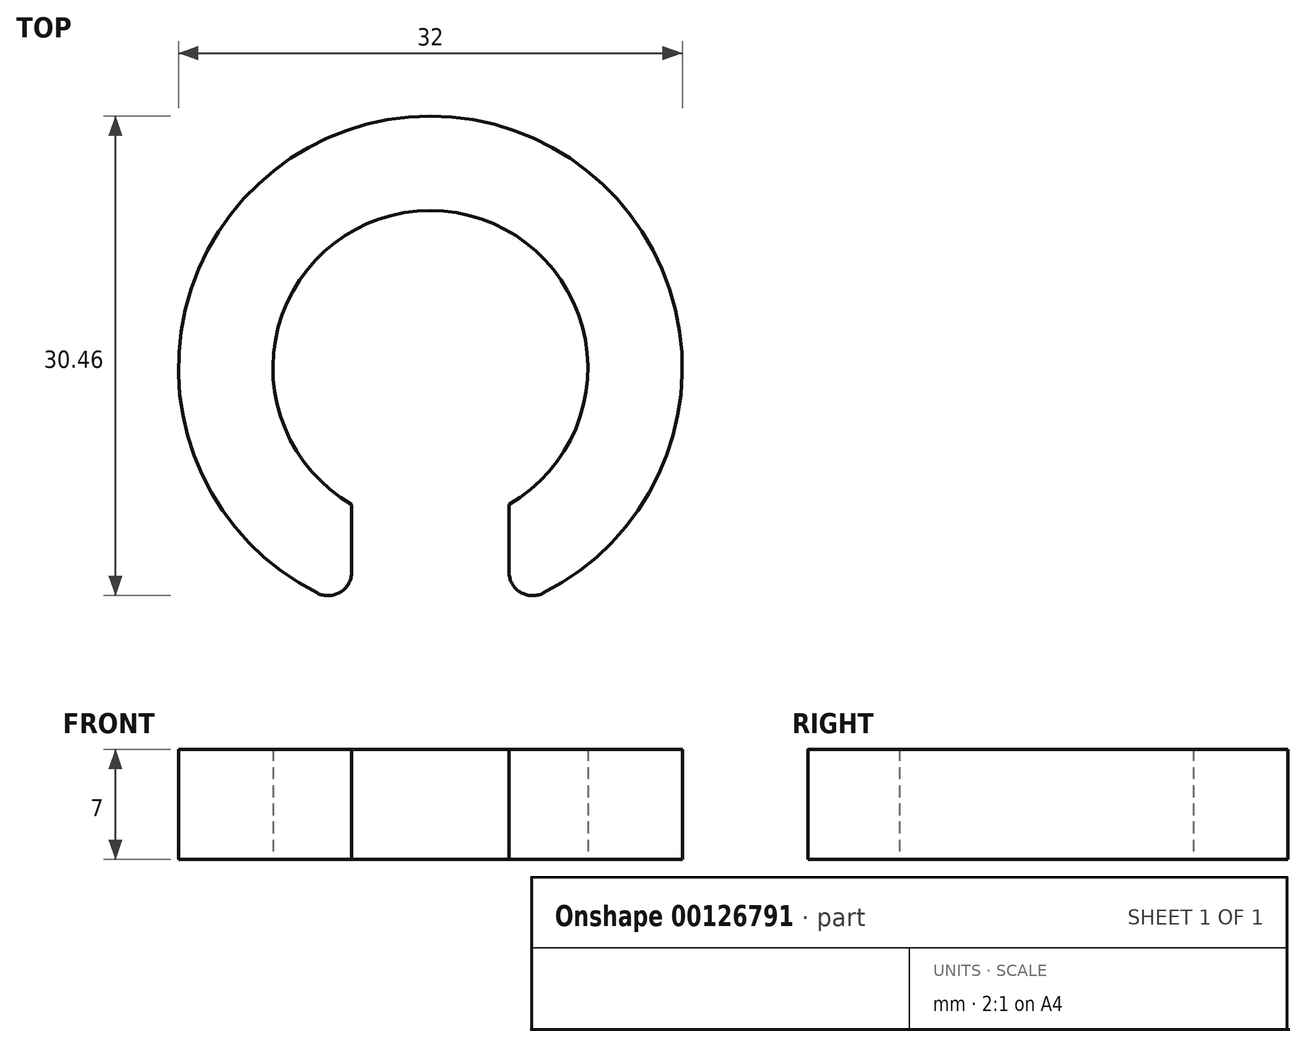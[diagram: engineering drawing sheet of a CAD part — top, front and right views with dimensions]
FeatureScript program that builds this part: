
annotation { "Feature Type Name" : "Feature", "Feature Type Description" : "" }
export const myFeature = defineFeature(function(context is Context, id is Id, definition is map)
    precondition{}
    {
        {
            var Q0;
            Q0=qCreatedBy(makeId("Top.planeOp"),FACE);
            var sketch = newSketch(context, id + "F0", { "sketchPlane" : qUnion([Q0])});
            skCircle(sketch, "E0", {"center": v(0, 0) * mm, "radius": 10 * mm});
            skCircle(sketch, "E1.0", {"center": v(0, 0) * mm, "radius": 16 * mm});
            skLineSegment(sketch, "E2", {"start": v(0, 0) * mm, "end": v(0, -20) * mm, "construction": true});
            skCircle(sketch, "E3", {"center": v(0, 0) * mm, "radius": 6.64 * mm, "construction": true});
            skLineSegment(sketch, "E4.0", {"start": v(-5, -8.66) * mm, "end": v(-5, -15.2) * mm});
            skLineSegment(sketch, "E5.trimOffspring", {"start": v(5, -8.66) * mm, "end": v(5, -15.2) * mm});
            skSolve(sketch);
        }
        {
            var Q0;
            {var subQ0=sQuery(id+"F0.wireOp",EDGE,"E4.0");Q0=makeQuery(id+"F0.imprint","IMPRINT",FACE,{"disambiguationData":[TD([[makeQuery(id+"F0.imprint","IMPRINT",EDGE,{"derivedFrom":subQ0}),-1.0]])]});}
            extrude(context, id + "F1", {"entities" : qUnion([Q0]), "depth" : 7 * mm});
        }
        {
            var Q0;
            Q0=makeQuery(id+"F1.opExtrude","SWEPT_EDGE",EDGE,{"disambiguationData":[OSD([sQuery(id+"F0.wireOp",EDGE,"E1.0"),sQuery(id+"F0.wireOp",EDGE,"E4.0")])]});
            var Q1;
            Q1=makeQuery(id+"F1.opExtrude","SWEPT_EDGE",EDGE,{"disambiguationData":[OSD([sQuery(id+"F0.wireOp",EDGE,"E1.0"),sQuery(id+"F0.wireOp",EDGE,"E5.trimOffspring")])]});
            fillet(context, id + "F2", {"entities" : qUnion([Q0, Q1]), "radius" : 1.5 * mm, "tangentPropagation" : true, "allowEdgeOverflow" : false});
        }
    });
